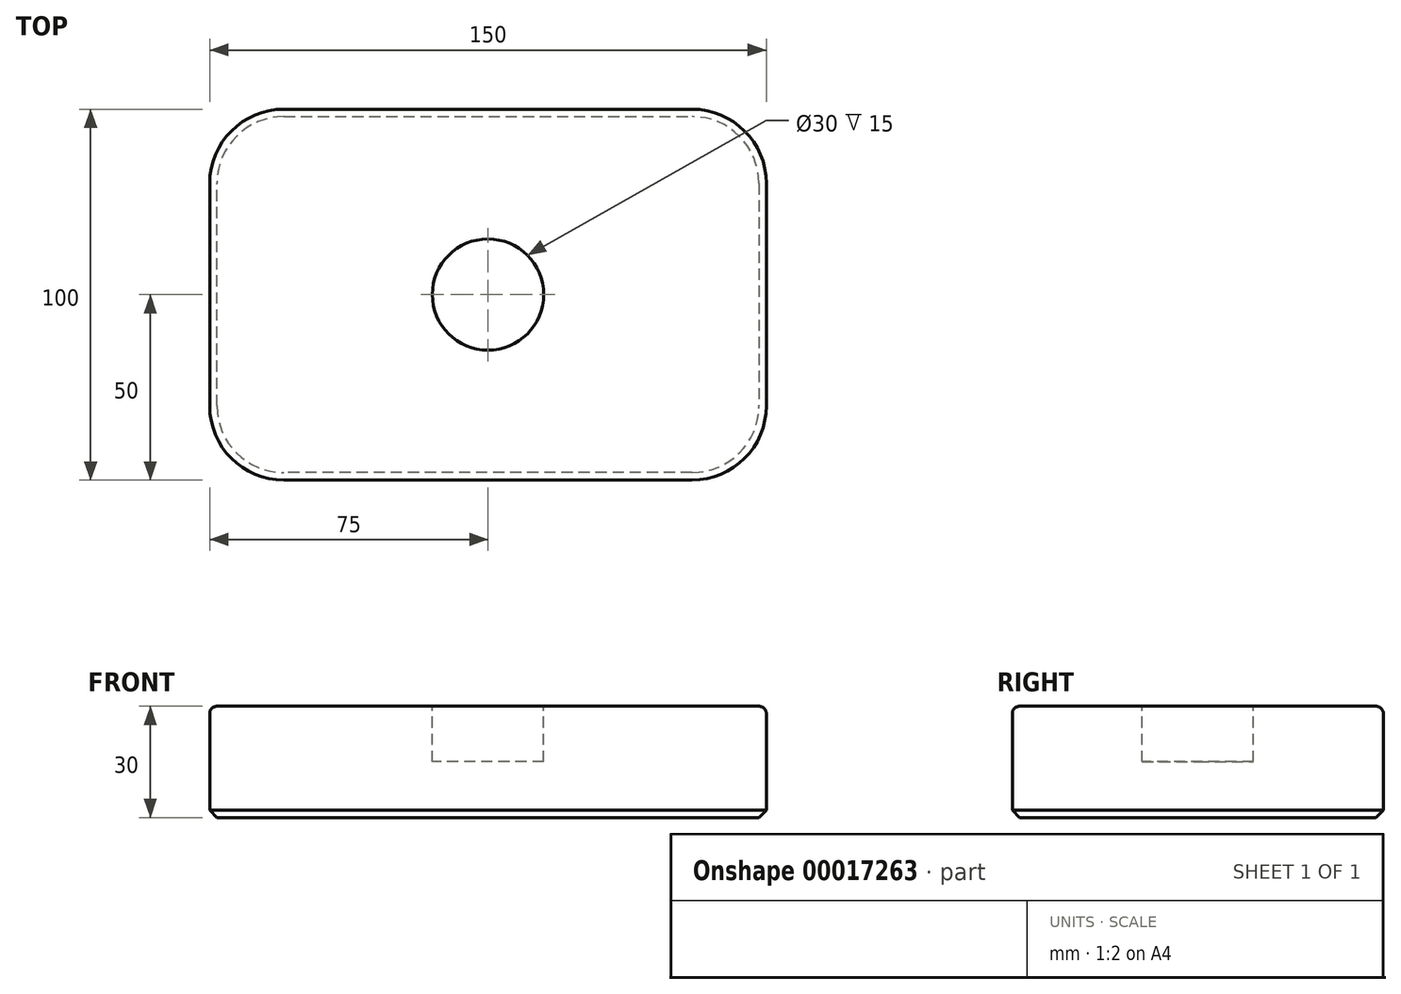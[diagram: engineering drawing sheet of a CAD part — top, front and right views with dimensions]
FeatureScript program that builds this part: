
annotation { "Feature Type Name" : "Feature", "Feature Type Description" : "" }
export const myFeature = defineFeature(function(context is Context, id is Id, definition is map)
    precondition{}
    {
        {
            var Q0;
            Q0=qCreatedBy(makeId("Top.planeOp"),FACE);
            var sketch = newSketch(context, id + "F0", { "sketchPlane" : qUnion([Q0])});
            skLineSegment(sketch, "E0.rect.bottom", {"start": v(-55, -50) * mm, "end": v(55, -50) * mm});
            skLineSegment(sketch, "E0.rect.top", {"start": v(-55, 50) * mm, "end": v(55, 50) * mm});
            skLineSegment(sketch, "E0.rect.left", {"start": v(-75, -30) * mm, "end": v(-75, 30) * mm});
            skLineSegment(sketch, "E0.rect.right", {"start": v(75, -30) * mm, "end": v(75, 30) * mm});
            skPoint(sketch, "E1.visualSharp", {"position": v(-75, 50) * mm});
            skArc(sketch, "E1.filletArc", {"start": v(-55, 50) * mm, "mid": v(-69.14, 44.14) * mm, "end": v(-75, 30) * mm});
            skPoint(sketch, "E2.visualSharp", {"position": v(75, 50) * mm});
            skArc(sketch, "E2.filletArc", {"start": v(75, 30) * mm, "mid": v(69.14, 44.14) * mm, "end": v(55, 50) * mm});
            skPoint(sketch, "E3.visualSharp", {"position": v(75, -50) * mm});
            skArc(sketch, "E3.filletArc", {"start": v(55, -50) * mm, "mid": v(69.14, -44.14) * mm, "end": v(75, -30) * mm});
            skPoint(sketch, "E4.visualSharp", {"position": v(-75, -50) * mm});
            skArc(sketch, "E4.filletArc", {"start": v(-75, -30) * mm, "mid": v(-69.14, -44.14) * mm, "end": v(-55, -50) * mm});
            skPoint(sketch, "E5", {"position": v(0, 0) * mm});
            skSolve(sketch);
        }
        {
            var Q0;
            Q0 = qSketchRegion(id + "F0", true);
            extrude(context, id + "F1", {"entities" : qUnion([Q0]), "depth" : 30 * mm});
        }
        {
            var Q0;
            Q0=makeQuery(id+"F1.opExtrude","CAP_EDGE",EDGE,{"disambiguationData":[OSD([sQuery(id+"F0.wireOp",EDGE,"E4.filletArc")])],"isStart":false});
            fillet(context, id + "F2", {"entities" : qUnion([Q0]), "radius" : 2 * mm, "tangentPropagation" : true, "allowEdgeOverflow" : false});
        }
        {
            var Q0;
            Q0=makeQuery(id+"F1.opExtrude","CAP_EDGE",EDGE,{"disambiguationData":[OSD([sQuery(id+"F0.wireOp",EDGE,"E0.rect.bottom")])],"isStart":true});
            chamfer(context, id + "F3", {"entities" : qUnion([Q0]), "width" : 2 * mm, "tangentPropagation" : true});
        }
        {
            var Q0;
            Q0=makeQuery(id+"F1.opExtrude","CAP_FACE",FACE,{"disambiguationData":[OSD([sQuery(id+"F0.wireOp",EDGE,"E0.rect.bottom"),sQuery(id+"F0.wireOp",EDGE,"E0.rect.top"),sQuery(id+"F0.wireOp",EDGE,"E0.rect.left"),sQuery(id+"F0.wireOp",EDGE,"E0.rect.right"),sQuery(id+"F0.wireOp",EDGE,"E1.filletArc"),sQuery(id+"F0.wireOp",EDGE,"E2.filletArc"),sQuery(id+"F0.wireOp",EDGE,"E3.filletArc"),sQuery(id+"F0.wireOp",EDGE,"E4.filletArc")])],"isStart":false});
            var sketch = newSketch(context, id + "F4", { "sketchPlane" : qUnion([Q0])});
            skCircle(sketch, "E6", {"center": v(0, 0) * mm, "radius": 15 * mm});
            skSolve(sketch);
        }
        {
            var Q0;
            Q0=makeQuery(id+"F4.imprint","IMPRINT",FACE,{"disambiguationData":[TD([[makeQuery(id+"F4.imprint","IMPRINT",EDGE,{"derivedFrom":sQuery(id+"F4.wireOp",EDGE,"E6")}),1.0]])]});
            extrude(context, id + "F5", {"entities" : qUnion([Q0]), "operationType" : NewBodyOperationType.REMOVE, "oppositeDirection" : true, "depth" : 15 * mm});
        }
    });
